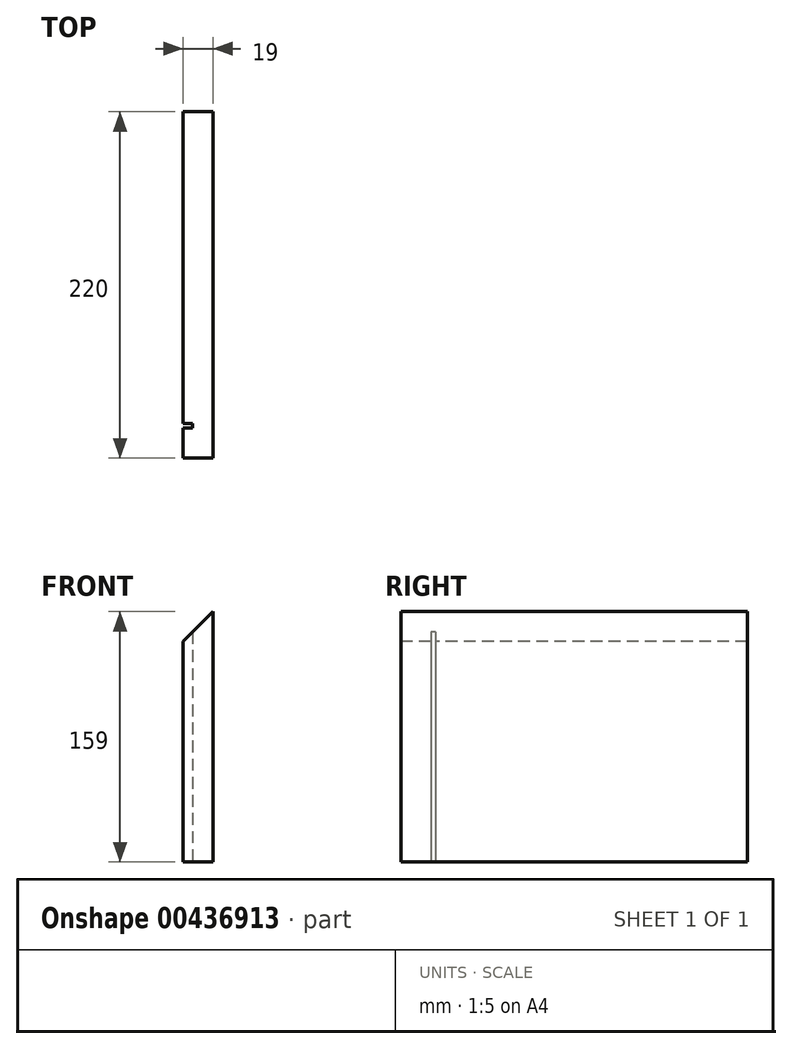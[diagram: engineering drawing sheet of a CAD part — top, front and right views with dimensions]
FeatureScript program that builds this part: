
annotation { "Feature Type Name" : "Feature", "Feature Type Description" : "" }
export const myFeature = defineFeature(function(context is Context, id is Id, definition is map)
    precondition{}
    {
        {
            var Q0;
            Q0=qCreatedBy(makeId("Front.planeOp"),FACE);
            var sketch = newSketch(context, id + "F0", { "sketchPlane" : qUnion([Q0])});
            skLineSegment(sketch, "E0", {"start": v(0, 0) * mm, "end": v(19, 0) * mm});
            skLineSegment(sketch, "E1", {"start": v(19, 0) * mm, "end": v(19, 159) * mm});
            skLineSegment(sketch, "E2", {"start": v(19, 159) * mm, "end": v(0, 140) * mm});
            skLineSegment(sketch, "E3", {"start": v(0, 140) * mm, "end": v(0, 0) * mm});
            skSolve(sketch);
        }
        {
            var Q0;
            Q0 = qSketchRegion(id + "F0", true);
            extrude(context, id + "F1", {"entities" : qUnion([Q0]), "oppositeDirection" : true, "depth" : 220 * mm});
        }
        {
            var Q0;
            Q0=makeQuery(id+"F1.opExtrude","SWEPT_FACE",FACE,{"disambiguationData":[OSD([sQuery(id+"F0.wireOp",EDGE,"E0")])]});
            var sketch = newSketch(context, id + "F2", { "sketchPlane" : qUnion([Q0])});
            skLineSegment(sketch, "E4.bottom", {"start": v(0, -19) * mm, "end": v(6, -19) * mm});
            skLineSegment(sketch, "E4.top", {"start": v(0, -22) * mm, "end": v(6, -22) * mm});
            skLineSegment(sketch, "E4.left", {"start": v(0, -19) * mm, "end": v(0, -22) * mm});
            skLineSegment(sketch, "E4.right", {"start": v(6, -19) * mm, "end": v(6, -22) * mm});
            skSolve(sketch);
        }
        {
            var Q0;
            Q0 = qSketchRegion(id + "F2", true);
            extrude(context, id + "F3", {"entities" : qUnion([Q0]), "operationType" : NewBodyOperationType.REMOVE, "endBound" : BoundingType.THROUGH_ALL, "oppositeDirection" : true, "depth" : 25 * mm});
        }
    });
